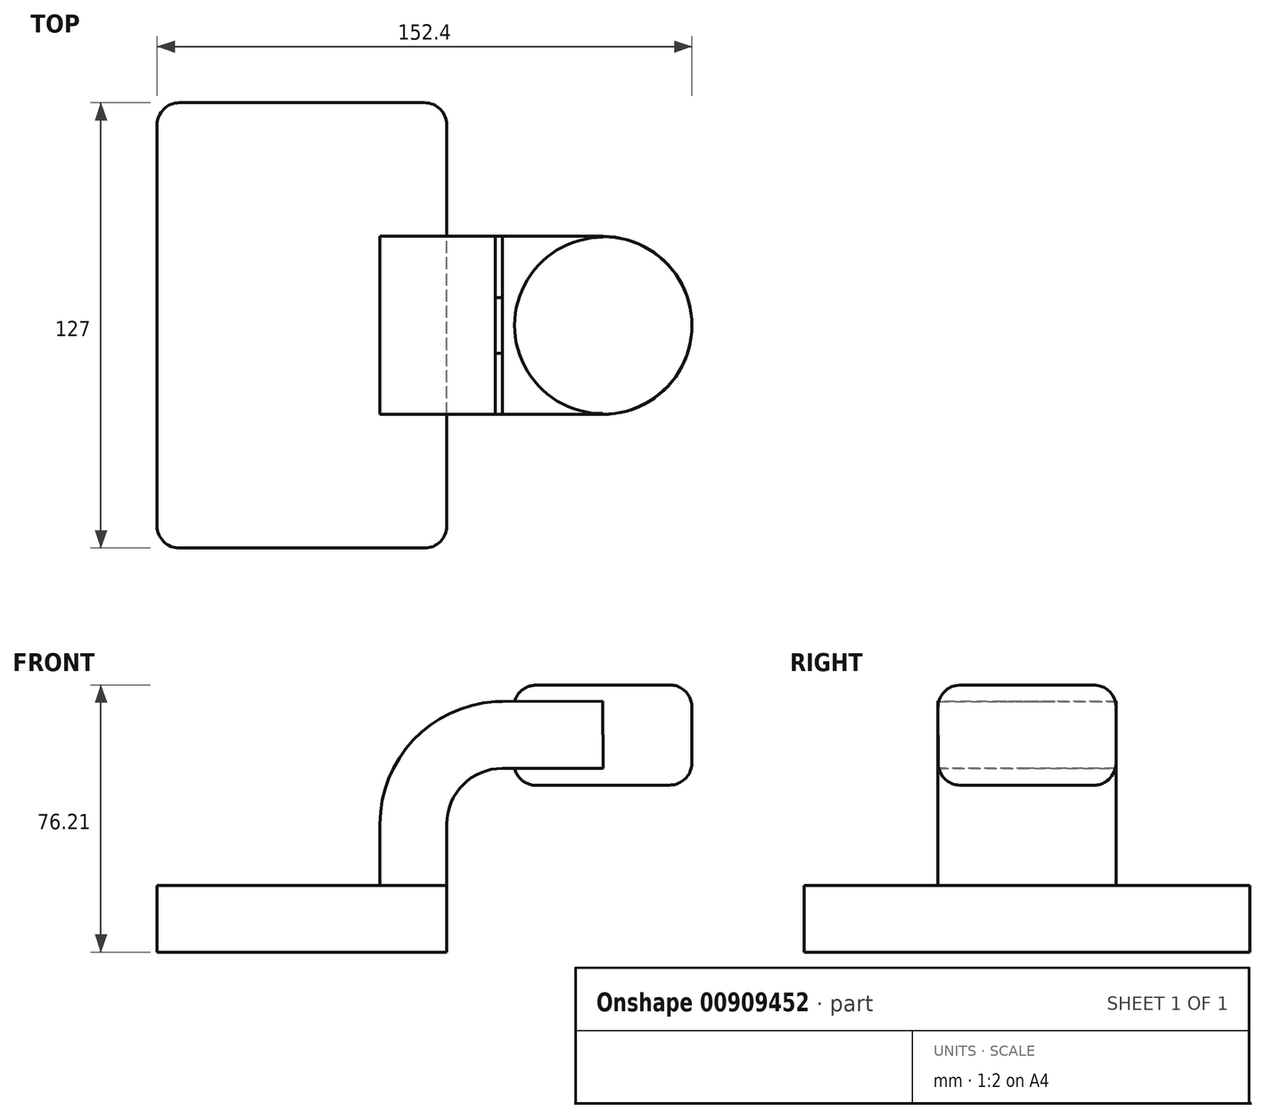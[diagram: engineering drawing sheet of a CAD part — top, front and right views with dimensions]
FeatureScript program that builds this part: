
annotation { "Feature Type Name" : "Feature", "Feature Type Description" : "" }
export const myFeature = defineFeature(function(context is Context, id is Id, definition is map)
    precondition{}
    {
        {
            var Q0;
            Q0=qCreatedBy(makeId("Front.planeOp"),FACE);
            var sketch = newSketch(context, id + "F0", { "sketchPlane" : qUnion([Q0])});
            skLineSegment(sketch, "E0.bottom", {"start": v(41.28, -9.52) * mm, "end": v(-41.28, -9.53) * mm});
            skLineSegment(sketch, "E0.top", {"start": v(41.28, 9.53) * mm, "end": v(-41.28, 9.53) * mm});
            skLineSegment(sketch, "E0.left", {"start": v(41.28, -9.52) * mm, "end": v(41.28, 9.53) * mm});
            skLineSegment(sketch, "E0.right", {"start": v(-41.28, -9.53) * mm, "end": v(-41.28, 9.53) * mm});
            skPoint(sketch, "E0.middle", {"position": v(0, 0) * mm});
            skLineSegment(sketch, "E1.bottom", {"start": v(60.32, 38.1) * mm, "end": v(111.12, 38.1) * mm});
            skLineSegment(sketch, "E1.top", {"start": v(60.32, 66.68) * mm, "end": v(111.12, 66.68) * mm});
            skLineSegment(sketch, "E1.left", {"start": v(60.32, 38.1) * mm, "end": v(60.32, 66.68) * mm});
            skLineSegment(sketch, "E1.right", {"start": v(111.12, 38.1) * mm, "end": v(111.12, 66.68) * mm});
            skPoint(sketch, "E1.middle", {"position": v(85.72, 52.39) * mm});
            skLineSegment(sketch, "E2", {"start": v(41.28, 9.53) * mm, "end": v(41.28, 27) * mm});
            skArc(sketch, "E3", {"start": v(41.27, 27) * mm, "mid": v(45.92, 38.23) * mm, "end": v(57.15, 42.88) * mm});
            skLineSegment(sketch, "E4", {"start": v(57.15, 42.88) * mm, "end": v(85.8, 42.88) * mm});
            skArc(sketch, "E5.1", {"start": v(22.23, 27) * mm, "mid": v(32.45, 51.7) * mm, "end": v(57.15, 61.93) * mm});
            skLineSegment(sketch, "E5.2", {"start": v(22.22, 9.53) * mm, "end": v(22.22, 27) * mm});
            skLineSegment(sketch, "E6", {"start": v(85.73, 66.68) * mm, "end": v(85.8, 38.1) * mm});
            skLineSegment(sketch, "E7", {"start": v(57.15, 61.93) * mm, "end": v(85.74, 62) * mm});
            skFitSpline(sketch, "E8", {"points": [v(-41.28, 9.53) * mm, v(57.15, 61.93) * mm], "startDerivative": vector(0, 80.29) * mm, "endDerivative": vector(101.18, 1.62) * mm});
            skSolve(sketch);
        }
        {
            var Q0;
            Q0=makeQuery(id+"F0.imprint","IMPRINT",FACE,{"disambiguationData":[TD([[makeQuery(id+"F0.imprint","IMPRINT",EDGE,{"derivedFrom":sQuery(id+"F0.wireOp",EDGE,"E0.bottom")}),-1.0]])]});
            extrude(context, id + "F1", {"entities" : qUnion([Q0]), "endBound" : BoundingType.SYMMETRIC, "depth" : 127 * mm, "offsetDistance" : 25.4 * mm});
        }
        {
            var Q0;
            {var subQ1=sQuery(id+"F0.wireOp",EDGE,"E2");Q0=makeQuery(id+"F0.imprint","IMPRINT",FACE,{"disambiguationData":[TD([[makeQuery(id+"F0.imprint","IMPRINT",EDGE,{"derivedFrom":subQ1}),1.0]])]});}
            var Q1;
            {var subQ0=sQuery(id+"F0.wireOp",EDGE,"E4");var subQ1=sQuery(id+"F0.wireOp",EDGE,"E1.left");var subQ2=makeQuery(id+"F0.imprint","INTERSECT",VERTEX,{"derivedFrom":[subQ1,subQ0]});Q1=makeQuery(id+"F0.imprint","IMPRINT",FACE,{"disambiguationData":[TD([[makeQuery(id+"F0.imprint","IMPRINT",EDGE,{"disambiguationData":[TD([[subQ2,-1.0]])],"derivedFrom":subQ1}),-1.0]])]});}
            var Q2;
            {var subQ3=sQuery(id+"F0.wireOp",EDGE,"E6");var subQ5=sQuery(id+"F0.wireOp",EDGE,"E5.0");var subQ7=makeQuery(id+"F0.imprint","INTERSECT",VERTEX,{"derivedFrom":[subQ5,subQ3]});Q2=makeQuery(id+"F0.imprint","IMPRINT",FACE,{"disambiguationData":[TD([[makeQuery(id+"F0.imprint","IMPRINT",EDGE,{"disambiguationData":[TD([[subQ7,1.0]])],"derivedFrom":subQ5}),1.0]])]});}
            extrude(context, id + "F2", {"entities" : qUnion([Q0, Q1, Q2]), "endBound" : BoundingType.SYMMETRIC, "depth" : 50.8 * mm, "offsetDistance" : 25.4 * mm});
        }
        {
            var Q0;
            {var subQ0=sQuery(id+"F0.wireOp",EDGE,"E5.1");Q0=makeQuery(id+"F0.imprint","IMPRINT",FACE,{"disambiguationData":[TD([[makeQuery(id+"F0.imprint","IMPRINT",EDGE,{"derivedFrom":subQ0}),1.0]])]});}
            extrude(context, id + "F3", {"entities" : qUnion([Q0]), "endBound" : BoundingType.SYMMETRIC, "depth" : 15.88 * mm, "offsetDistance" : 25.4 * mm});
        }
        {
            var Q0;
            {var subQ4=sQuery(id+"F0.wireOp",EDGE,"E1.right");Q0=makeQuery(id+"F0.imprint","IMPRINT",FACE,{"disambiguationData":[TD([[makeQuery(id+"F0.imprint","IMPRINT",EDGE,{"derivedFrom":subQ4}),1.0]])]});}
            var Q1;
            Q1=sQuery(id+"F0.wireOp",EDGE,"E6");
            revolve(context, id + "F4", {"operationType" : NewBodyOperationType.ADD, "surfaceOperationType" : NewSurfaceOperationType.NEW, "entities" : qUnion([Q0]), "axis" : qUnion([Q1]), "revolveType" : RevolveType.FULL});
        }
        {
            var Q0;
            Q0=makeQuery(id+"F1.opExtrude","CAP_EDGE",EDGE,{"disambiguationData":[OSD([sQuery(id+"F0.wireOp",EDGE,"E0.left")])],"isStart":false});
            var Q1;
            Q1=makeQuery(id+"F1.opExtrude","CAP_EDGE",EDGE,{"disambiguationData":[OSD([sQuery(id+"F0.wireOp",EDGE,"E0.right")])],"isStart":false});
            var Q2;
            Q2=makeQuery(id+"F1.opExtrude","CAP_EDGE",EDGE,{"disambiguationData":[OSD([sQuery(id+"F0.wireOp",EDGE,"E0.left")])],"isStart":true});
            var Q3;
            Q3=makeQuery(id+"F1.opExtrude","CAP_EDGE",EDGE,{"disambiguationData":[OSD([sQuery(id+"F0.wireOp",EDGE,"E0.right")])],"isStart":true});
            var Q4;
            Q4=makeQuery(id+"F4.opRevolve","SWEPT_EDGE",EDGE,{"disambiguationData":[OSD([sQuery(id+"F0.wireOp",EDGE,"E1.top"),sQuery(id+"F0.wireOp",EDGE,"E1.right")])]});
            var Q5;
            Q5=makeQuery(id+"F4.opRevolve","SWEPT_EDGE",EDGE,{"disambiguationData":[OSD([sQuery(id+"F0.wireOp",EDGE,"E1.bottom"),sQuery(id+"F0.wireOp",EDGE,"E1.right")])]});
            fillet(context, id + "F5", {"entities" : qUnion([Q0, Q1, Q2, Q3, Q4, Q5]), "radius" : 6.35 * mm, "tangentPropagation" : true, "allowEdgeOverflow" : false});
        }
    });
